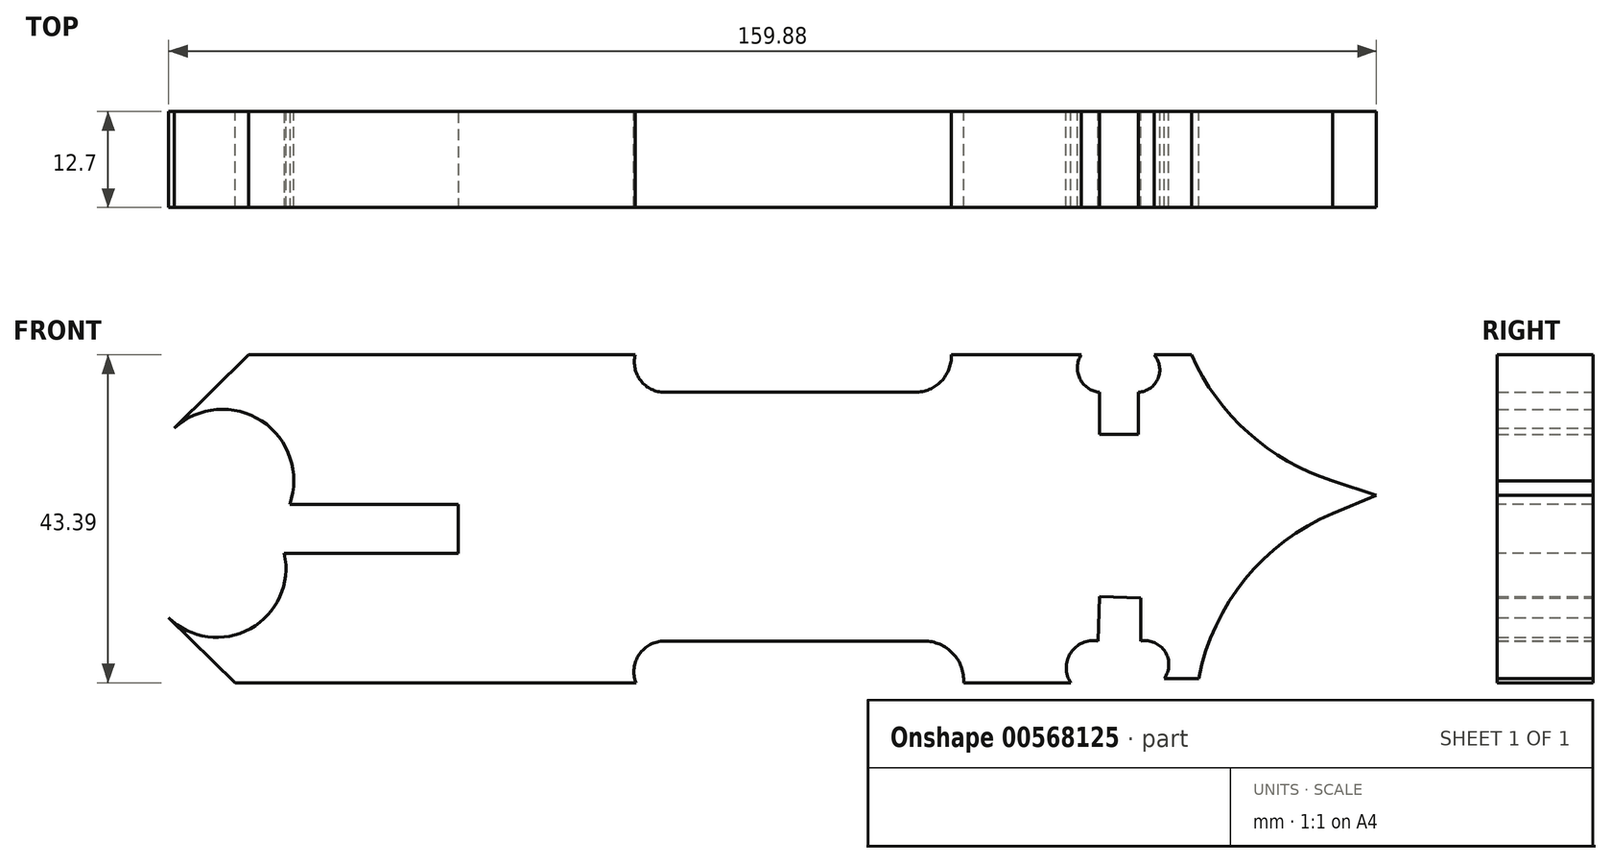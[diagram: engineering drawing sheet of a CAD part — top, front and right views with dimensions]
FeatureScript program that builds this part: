
annotation { "Feature Type Name" : "Feature", "Feature Type Description" : "" }
export const myFeature = defineFeature(function(context is Context, id is Id, definition is map)
    precondition{}
    {
        {
            var Q0;
            Q0=qCreatedBy(makeId("Front.planeOp"),FACE);
            var sketch = newSketch(context, id + "F0", { "sketchPlane" : qUnion([Q0])});
            skLineSegment(sketch, "E0", {"start": v(-55.96, 13.02) * mm, "end": v(-45.72, 23.12) * mm});
            skLineSegment(sketch, "E1", {"start": v(-45.72, 23.12) * mm, "end": v(5.47, 23.12) * mm});
            skLineSegment(sketch, "E2", {"start": v(9.34, 18.18) * mm, "end": v(42.53, 18.18) * mm});
            skLineSegment(sketch, "E3", {"start": v(47.32, 23.12) * mm, "end": v(64.5, 23.12) * mm});
            skLineSegment(sketch, "E4", {"start": v(66.91, 18.18) * mm, "end": v(66.91, 12.58) * mm});
            skLineSegment(sketch, "E5", {"start": v(66.91, 12.58) * mm, "end": v(72.1, 12.58) * mm});
            skLineSegment(sketch, "E6", {"start": v(72.1, 12.58) * mm, "end": v(72.1, 18.18) * mm});
            skLineSegment(sketch, "E7", {"start": v(74.17, 23.12) * mm, "end": v(79.1, 23.12) * mm});
            skPoint(sketch, "E8.end.orphan", {"position": v(5.47, -11.02) * mm});
            skLineSegment(sketch, "E9", {"start": v(5.57, -20.27) * mm, "end": v(-47.5, -20.27) * mm});
            skLineSegment(sketch, "E10", {"start": v(-47.5, -20.27) * mm, "end": v(-56.3, -11.64) * mm});
            skPoint(sketch, "E11.end.orphan", {"position": v(-42.35, 0) * mm});
            skPoint(sketch, "E12.end.orphan", {"position": v(9.34, -12.17) * mm});
            skPoint(sketch, "E12.start.orphan", {"position": v(42.53, -13.05) * mm});
            skPoint(sketch, "E13.end.orphan", {"position": v(47.32, -12.17) * mm});
            skLineSegment(sketch, "E14", {"start": v(9.34, -14.75) * mm, "end": v(43.72, -14.75) * mm});
            skLineSegment(sketch, "E15", {"start": v(48.94, -20.27) * mm, "end": v(63.13, -20.27) * mm});
            skPoint(sketch, "E16.end.orphan", {"position": v(64.5, -12.17) * mm});
            skPoint(sketch, "E17.end.orphan", {"position": v(66.91, -11.02) * mm});
            skPoint(sketch, "E18.end.orphan", {"position": v(66.91, -4.27) * mm});
            skPoint(sketch, "E19.end.orphan", {"position": v(72.1, -10.26) * mm});
            skPoint(sketch, "E20.end.orphan", {"position": v(74.17, -11.02) * mm});
            skLineSegment(sketch, "E21", {"start": v(66.71, -14.75) * mm, "end": v(66.91, -8.86) * mm});
            skLineSegment(sketch, "E22", {"start": v(66.91, -8.86) * mm, "end": v(72.39, -9.05) * mm});
            skLineSegment(sketch, "E23", {"start": v(72.39, -9.05) * mm, "end": v(72.39, -14.75) * mm});
            skLineSegment(sketch, "E24", {"start": v(75.49, -19.7) * mm, "end": v(80.06, -19.7) * mm});
            skPoint(sketch, "E25.orphan", {"position": v(79.1, -11.02) * mm});
            skArc(sketch, "E26", {"start": v(-42.35, 0) * mm, "mid": v(-42.65, 13.32) * mm, "end": v(-55.96, 13.02) * mm});
            skArc(sketch, "E27", {"start": v(-56.3, -11.64) * mm, "mid": v(-44.06, -12.13) * mm, "end": v(-42.35, 0) * mm});
            skArc(sketch, "E28", {"start": v(5.47, 23.12) * mm, "mid": v(6.2, 19.7) * mm, "end": v(9.34, 18.18) * mm});
            skArc(sketch, "E29", {"start": v(9.34, -14.75) * mm, "mid": v(6, -16.51) * mm, "end": v(5.57, -20.27) * mm});
            skArc(sketch, "E30", {"start": v(42.53, 18.18) * mm, "mid": v(45.98, 19.63) * mm, "end": v(47.32, 23.12) * mm});
            skArc(sketch, "E31", {"start": v(48.94, -20.27) * mm, "mid": v(47.52, -16.38) * mm, "end": v(43.72, -14.75) * mm});
            skArc(sketch, "E32", {"start": v(64.5, 23.12) * mm, "mid": v(64.33, 19.98) * mm, "end": v(66.91, 18.18) * mm});
            skArc(sketch, "E33", {"start": v(66.71, -14.75) * mm, "mid": v(63.1, -16.32) * mm, "end": v(63.13, -20.27) * mm});
            skArc(sketch, "E34", {"start": v(72.1, 18.18) * mm, "mid": v(74.67, 20) * mm, "end": v(74.17, 23.12) * mm});
            skArc(sketch, "E35", {"start": v(75.49, -19.7) * mm, "mid": v(75.62, -16.18) * mm, "end": v(72.39, -14.75) * mm});
            skPoint(sketch, "E36.end.orphan", {"position": v(93.01, -0.42) * mm});
            skPoint(sketch, "E37.start.orphan", {"position": v(93.01, 8.43) * mm});
            skArc(sketch, "E38", {"start": v(97.79, 2.11) * mm, "mid": v(86.18, -6.57) * mm, "end": v(80.06, -19.7) * mm});
            skLineSegment(sketch, "E39", {"start": v(97.79, 2.11) * mm, "end": v(103.58, 4.54) * mm});
            skLineSegment(sketch, "E40", {"start": v(103.58, 4.54) * mm, "end": v(97.77, 6.46) * mm});
            skArc(sketch, "E41", {"start": v(79.1, 23.12) * mm, "mid": v(86.66, 12.8) * mm, "end": v(97.77, 6.46) * mm});
            skSolve(sketch);
        }
        {
            var Q0;
            {var subQ0=sQuery(id+"F0.wireOp",EDGE,"E26");var subQ1=sQuery(id+"F0.wireOp",EDGE,"E0");var subQ2=makeQuery(id+"F0.imprint","INTERSECT",VERTEX,{"disambiguationData":[OD(0.0)],"derivedFrom":[subQ1,subQ0]});Q0=makeQuery(id+"F0.imprint","IMPRINT",FACE,{"disambiguationData":[TD([[makeQuery(id+"F0.imprint","IMPRINT",EDGE,{"disambiguationData":[TD([[subQ2,-1.0]])],"derivedFrom":subQ1}),1.0]])]});}
            var Q1;
            {var subQ4=sQuery(id+"F0.wireOp",EDGE,"E1");Q1=makeQuery(id+"F0.imprint","IMPRINT",FACE,{"disambiguationData":[TD([[makeQuery(id+"F0.imprint","IMPRINT",EDGE,{"derivedFrom":subQ4}),-1.0]])]});}
            extrude(context, id + "F1", {"entities" : qUnion([Q0, Q1]), "depth" : 12.7 * mm, "offsetDistance" : 25.4 * mm});
        }
        {
            var Q0;
            Q0=makeQuery(id+"F1.opExtrude","CAP_FACE",FACE,{"disambiguationData":[OSD([sQuery(id+"F0.wireOp",EDGE,"E0"),sQuery(id+"F0.wireOp",EDGE,"E1"),sQuery(id+"F0.wireOp",EDGE,"E2"),sQuery(id+"F0.wireOp",EDGE,"E3"),sQuery(id+"F0.wireOp",EDGE,"E4"),sQuery(id+"F0.wireOp",EDGE,"E5"),sQuery(id+"F0.wireOp",EDGE,"E6"),sQuery(id+"F0.wireOp",EDGE,"E7"),sQuery(id+"F0.wireOp",EDGE,"E9"),sQuery(id+"F0.wireOp",EDGE,"E10"),sQuery(id+"F0.wireOp",EDGE,"E14"),sQuery(id+"F0.wireOp",EDGE,"E15"),sQuery(id+"F0.wireOp",EDGE,"E21"),sQuery(id+"F0.wireOp",EDGE,"E22"),sQuery(id+"F0.wireOp",EDGE,"E23"),sQuery(id+"F0.wireOp",EDGE,"E24"),sQuery(id+"F0.wireOp",EDGE,"E26"),sQuery(id+"F0.wireOp",EDGE,"E27"),sQuery(id+"F0.wireOp",EDGE,"E28"),sQuery(id+"F0.wireOp",EDGE,"E29"),sQuery(id+"F0.wireOp",EDGE,"E30"),sQuery(id+"F0.wireOp",EDGE,"E31"),sQuery(id+"F0.wireOp",EDGE,"E32"),sQuery(id+"F0.wireOp",EDGE,"E33"),sQuery(id+"F0.wireOp",EDGE,"E34"),sQuery(id+"F0.wireOp",EDGE,"E35"),sQuery(id+"F0.wireOp",EDGE,"E38"),sQuery(id+"F0.wireOp",EDGE,"E39"),sQuery(id+"F0.wireOp",EDGE,"E40"),sQuery(id+"F0.wireOp",EDGE,"E41")])],"isStart":false});
            var sketch = newSketch(context, id + "F2", { "sketchPlane" : qUnion([Q0])});
            skLineSegment(sketch, "E42", {"start": v(-40.29, 3.34) * mm, "end": v(-17.95, 3.34) * mm});
            skPoint(sketch, "E43.end.orphan", {"position": v(-17.95, 0) * mm});
            skLineSegment(sketch, "E44", {"start": v(-17.95, 3.34) * mm, "end": v(-17.95, -3.17) * mm});
            skLineSegment(sketch, "E45", {"start": v(-17.95, -3.17) * mm, "end": v(-41, -3.17) * mm});
            skSolve(sketch);
        }
        {
            var Q0;
            {var subQ6=sQuery(id+"F2.wireOp",EDGE,"E42");Q0=makeQuery(id+"F2.imprint","IMPRINT",FACE,{"disambiguationData":[TD([[makeQuery(id+"F2.imprint","IMPRINT",EDGE,{"derivedFrom":subQ6}),-1.0]])]});}
            extrude(context, id + "F3", {"entities" : qUnion([Q0]), "operationType" : NewBodyOperationType.REMOVE, "oppositeDirection" : true, "depth" : 25.4 * mm, "offsetDistance" : 25.4 * mm});
        }
    });
